# Revit family: NXRC-UL924
name_source: partatom
category: Communication Devices
revit_build: Autodesk Revit 2014 (Build: 20130308_1515(x64)
units: mm (PartAtom-declared; Revit-internal decimal feet)

## types (1)
- NXRC-UL924
    Assembly Code = D5090
    Certification = Conforms with UL916 and Certified to CAN/CSA C22.2 No. 205-M1983
IC Approved
Title 24 compliance
    Default Elevation = 48 "
    Description = NX Emergency Lighting Room Controller, one single pole relay, one 0 - 10 dimmer, one color control channel
    Dimming = Class 2 0-10VDC, 60mA current sink capacity,
For use with low voltage, two-wire dimming ballast and LED drivers
    Features = Meets NFPA Article 700 requirements for emergency lighting
• Zero cross switching technology extends relay contact life
• Full range continuous dimming defaults to full ON
• Color channel defaults SpectraSync™ luminaires to full white to user
selected color
• Single Cat5 cable connection to other NX devices
• Override push-button and status LED
• 120/277/347 universal voltage
• Provision for remote test button or fire alarm interface
    Housing Material = Paint - Hubbell - Red
    L = 5.26 "
    Manufacturer = Hubbell Control Solutions
    Model = NXRC SERIES
    Standby Power = 120VAC: 1.2,277VAC: 1.5,347VAC: 1.5
    Type Comments = UL924 ROOM CONTROLLER
    URL = https://www.hubbell.com
    Voltage = 120/277/347 VAC
    Warranty = 5-Years Warranty
    Washer = Metal-Hubbell-Galvanized_Steel

## geometry (parser evidence)
native form markers: Sweep x1
no freeform markers — native parametric forms only
